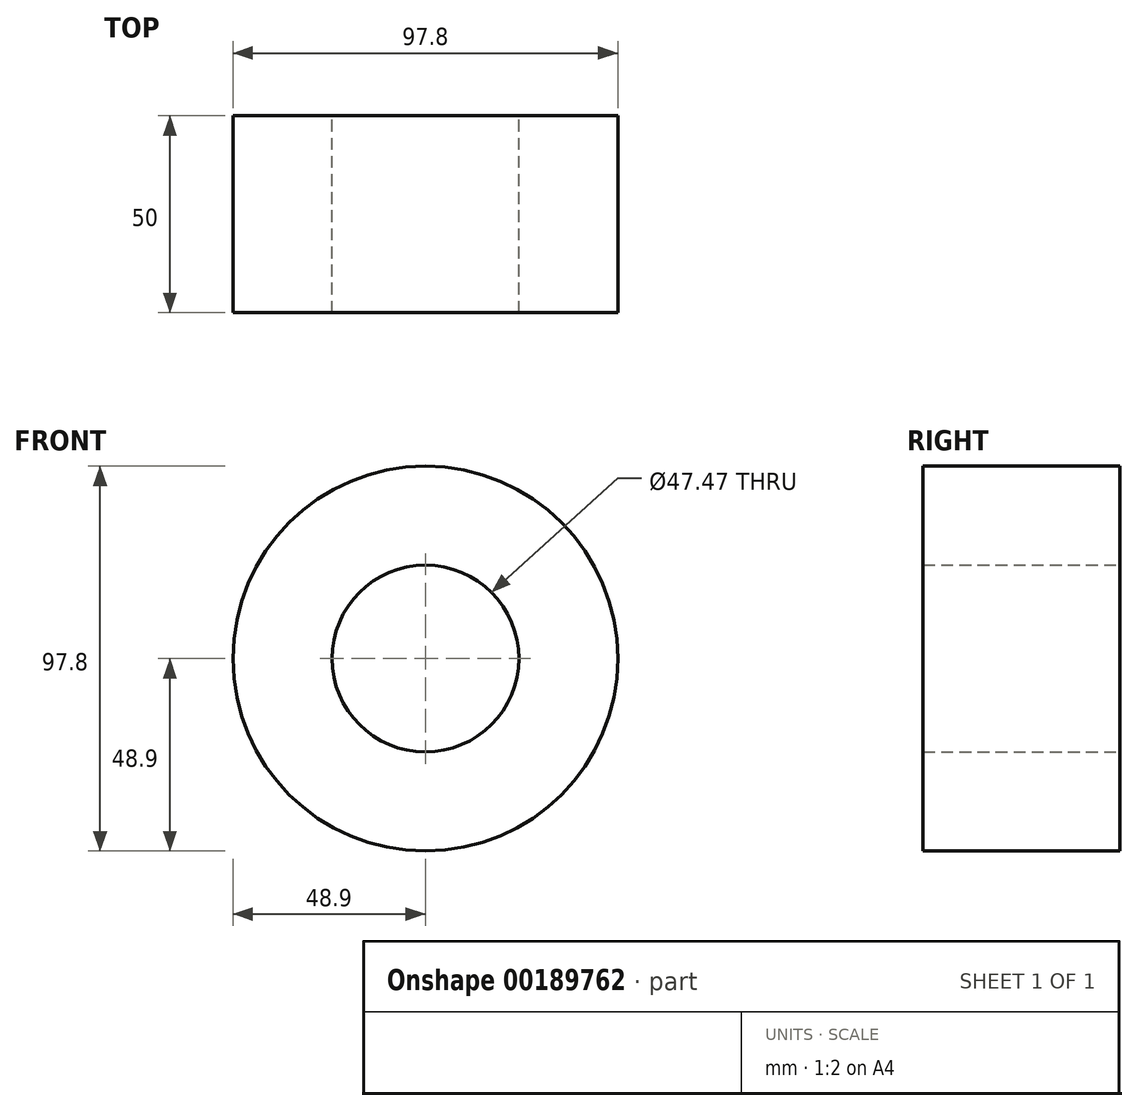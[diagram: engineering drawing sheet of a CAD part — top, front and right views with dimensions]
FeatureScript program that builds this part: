
annotation { "Feature Type Name" : "Feature", "Feature Type Description" : "" }
export const myFeature = defineFeature(function(context is Context, id is Id, definition is map)
    precondition{}
    {
        {
            var Q0;
            Q0=qCreatedBy(makeId("Front.planeOp"),FACE);
            var sketch = newSketch(context, id + "F0", { "sketchPlane" : qUnion([Q0])});
            skLineSegment(sketch, "E0", {"start": v(0, 0) * mm, "end": v(0, 50.01) * mm, "construction": true});
            skCircle(sketch, "E1", {"center": v(0, 0) * mm, "radius": 23.74 * mm});
            skCircle(sketch, "E2", {"center": v(0, 0) * mm, "radius": 48.9 * mm});
            skSolve(sketch);
        }
        {
            var Q0;
            Q0=makeQuery(id+"F0.imprint","IMPRINT",FACE,{"disambiguationData":[TD([[makeQuery(id+"F0.imprint","IMPRINT",EDGE,{"derivedFrom":sQuery(id+"F0.wireOp",EDGE,"E1")}),-1.0]])]});
            extrude(context, id + "F1", {"entities" : qUnion([Q0]), "depth" : 50 * mm});
        }
    });
